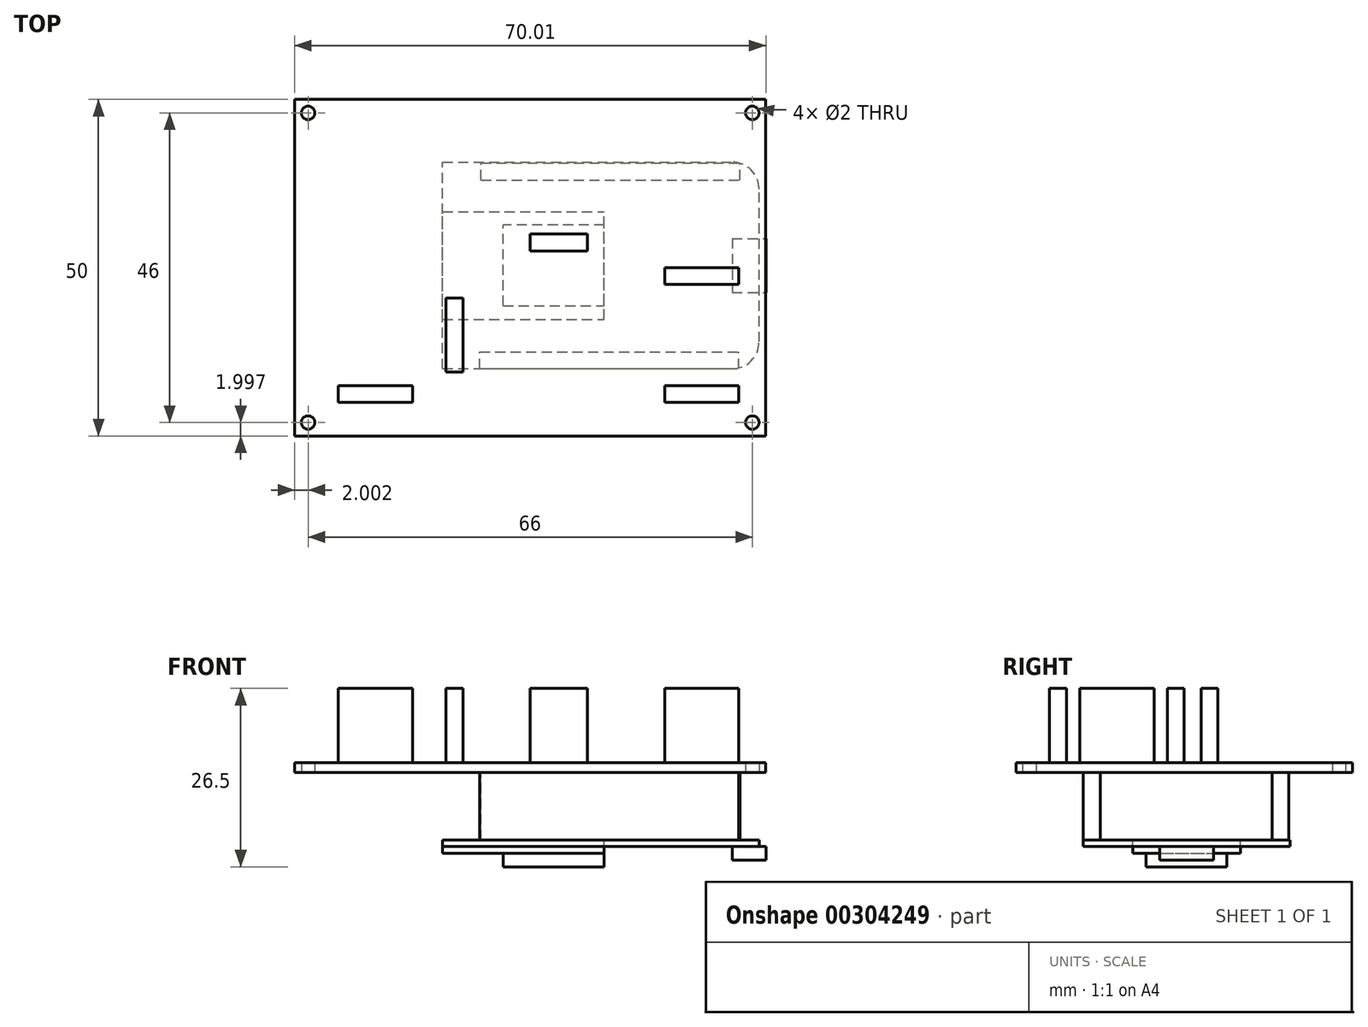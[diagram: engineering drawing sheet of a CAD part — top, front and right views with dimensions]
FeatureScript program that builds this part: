
annotation { "Feature Type Name" : "Feature", "Feature Type Description" : "" }
export const myFeature = defineFeature(function(context is Context, id is Id, definition is map)
    precondition{}
    {
        {
            var Q0;
            Q0=qCreatedBy(makeId("Top.planeOp"),FACE);
            var sketch = newSketch(context, id + "F0", { "sketchPlane" : qUnion([Q0])});
            skLineSegment(sketch, "E0.bottom", {"start": v(-0.7, -1.43) * mm, "end": v(69.3, -1.43) * mm});
            skLineSegment(sketch, "E0.top", {"start": v(-0.7, 48.57) * mm, "end": v(69.3, 48.57) * mm});
            skLineSegment(sketch, "E0.left", {"start": v(-0.7, -1.43) * mm, "end": v(-0.7, 48.57) * mm});
            skLineSegment(sketch, "E0.right", {"start": v(69.3, -1.43) * mm, "end": v(69.3, 48.57) * mm});
            skLineSegment(sketch, "E1.0", {"start": v(1.3, 46.57) * mm, "end": v(67.3, 46.57) * mm, "construction": true});
            skLineSegment(sketch, "E1.1", {"start": v(1.3, 0.57) * mm, "end": v(1.3, 46.57) * mm, "construction": true});
            skLineSegment(sketch, "E1.2", {"start": v(1.3, 0.57) * mm, "end": v(67.3, 0.57) * mm, "construction": true});
            skLineSegment(sketch, "E1.3", {"start": v(67.3, 0.57) * mm, "end": v(67.3, 46.57) * mm, "construction": true});
            skCircle(sketch, "E2", {"center": v(1.3, 0.57) * mm, "radius": 1 * mm});
            skCircle(sketch, "E3", {"center": v(1.3, 46.57) * mm, "radius": 1 * mm});
            skCircle(sketch, "E4", {"center": v(67.3, 46.57) * mm, "radius": 1 * mm});
            skCircle(sketch, "E5", {"center": v(67.3, 0.57) * mm, "radius": 1 * mm});
            skLineSegment(sketch, "E6.bottom", {"start": v(26.8, 8.57) * mm, "end": v(65.3, 8.57) * mm});
            skLineSegment(sketch, "E6.top", {"start": v(26.8, 11.07) * mm, "end": v(65.3, 11.07) * mm});
            skLineSegment(sketch, "E6.left", {"start": v(26.8, 8.57) * mm, "end": v(26.8, 11.07) * mm});
            skLineSegment(sketch, "E6.right", {"start": v(65.3, 8.57) * mm, "end": v(65.3, 11.07) * mm});
            skLineSegment(sketch, "E7.bottom", {"start": v(26.99, 36.6) * mm, "end": v(65.49, 36.6) * mm});
            skLineSegment(sketch, "E7.top", {"start": v(26.99, 39.1) * mm, "end": v(65.49, 39.1) * mm});
            skLineSegment(sketch, "E7.left", {"start": v(26.99, 36.6) * mm, "end": v(26.99, 39.1) * mm});
            skLineSegment(sketch, "E7.right", {"start": v(65.49, 36.6) * mm, "end": v(65.49, 39.1) * mm});
            skSolve(sketch);
        }
        {
            var Q0;
            Q0 = qSketchRegion(id + "F0", true);
            var Q1;
            Q1=makeQuery(id+"F0.imprint","IMPRINT",FACE,{"disambiguationData":[TD([[makeQuery(id+"F0.imprint","IMPRINT",EDGE,{"derivedFrom":sQuery(id+"F0.wireOp",EDGE,"E7.bottom")}),1.0]])]});
            var Q2;
            Q2=makeQuery(id+"F0.imprint","IMPRINT",FACE,{"disambiguationData":[TD([[makeQuery(id+"F0.imprint","IMPRINT",EDGE,{"derivedFrom":sQuery(id+"F0.wireOp",EDGE,"E6.bottom")}),1.0]])]});
            extrude(context, id + "F1", {"entities" : qUnion([Q0, Q1, Q2]), "depth" : 1.5 * mm});
        }
        {
            var Q0;
            Q0=makeQuery(id+"F0.imprint","IMPRINT",FACE,{"disambiguationData":[TD([[makeQuery(id+"F0.imprint","IMPRINT",EDGE,{"derivedFrom":sQuery(id+"F0.wireOp",EDGE,"E6.bottom")}),1.0]])]});
            var Q1;
            Q1=makeQuery(id+"F0.imprint","IMPRINT",FACE,{"disambiguationData":[TD([[makeQuery(id+"F0.imprint","IMPRINT",EDGE,{"derivedFrom":sQuery(id+"F0.wireOp",EDGE,"E7.bottom")}),1.0]])]});
            extrude(context, id + "F2", {"entities" : qUnion([Q0, Q1]), "oppositeDirection" : true, "depth" : 10 * mm});
        }
        {
            var Q0;
            Q0=makeQuery(id+"F2.opExtrude","CAP_FACE",FACE,{"disambiguationData":[OSD([sQuery(id+"F0.wireOp",EDGE,"E6.bottom"),sQuery(id+"F0.wireOp",EDGE,"E6.top"),sQuery(id+"F0.wireOp",EDGE,"E6.left"),sQuery(id+"F0.wireOp",EDGE,"E6.right")])],"isStart":false});
            var sketch = newSketch(context, id + "F3", { "sketchPlane" : qUnion([Q0])});
            skLineSegment(sketch, "E8.bottom", {"start": v(21.3, -8.57) * mm, "end": v(64.3, -8.57) * mm});
            skLineSegment(sketch, "E8.top", {"start": v(21.3, -39.27) * mm, "end": v(64.3, -39.27) * mm});
            skLineSegment(sketch, "E8.left", {"start": v(21.3, -8.57) * mm, "end": v(21.3, -39.27) * mm});
            skLineSegment(sketch, "E8.right", {"start": v(68.3, -12.57) * mm, "end": v(68.3, -35.27) * mm});
            skPoint(sketch, "E9.visualSharp", {"position": v(21.3, -8.57) * mm});
            skPoint(sketch, "E10.visualSharp", {"position": v(68.3, -8.57) * mm});
            skArc(sketch, "E10.filletArc", {"start": v(68.3, -12.57) * mm, "mid": v(67.13, -9.74) * mm, "end": v(64.3, -8.57) * mm});
            skPoint(sketch, "E11.visualSharp", {"position": v(68.3, -39.27) * mm});
            skArc(sketch, "E11.filletArc", {"start": v(64.3, -39.27) * mm, "mid": v(67.13, -38.1) * mm, "end": v(68.3, -35.27) * mm});
            skLineSegment(sketch, "E12.bottom", {"start": v(21.3, -15.92) * mm, "end": v(45.3, -15.92) * mm});
            skLineSegment(sketch, "E12.top", {"start": v(21.3, -31.92) * mm, "end": v(45.3, -31.92) * mm});
            skLineSegment(sketch, "E12.left", {"start": v(21.3, -15.92) * mm, "end": v(21.3, -31.92) * mm});
            skLineSegment(sketch, "E12.right", {"start": v(45.3, -15.92) * mm, "end": v(45.3, -31.92) * mm});
            skPoint(sketch, "E13", {"position": v(21.3, -23.92) * mm});
            skPoint(sketch, "E14", {"position": v(68.3, -23.92) * mm});
            skSolve(sketch);
        }
        {
            var Q0;
            Q0=makeQuery(id+"F3.imprint","IMPRINT",FACE,{"disambiguationData":[TD([[makeQuery(id+"F3.imprint","IMPRINT",EDGE,{"derivedFrom":sQuery(id+"F3.wireOp",EDGE,"E8.top")}),1.0]])]});
            var Q1;
            {var subQ1=makeQuery(id+"F2.opExtrude","CAP_EDGE",EDGE,{"disambiguationData":[OSD([sQuery(id+"F0.wireOp",EDGE,"E6.top")])],"isStart":false});Q1=makeQuery(id+"F3.imprint","IMPRINT",FACE,{"disambiguationData":[TD([[makeQuery(id+"F3.imprint","IMPRINT",EDGE,{"derivedFrom":subQ1}),1.0]])]});}
            var Q2;
            Q2=makeQuery(id+"F3.imprint","IMPRINT",FACE,{"disambiguationData":[TD([[makeQuery(id+"F3.imprint","IMPRINT",EDGE,{"derivedFrom":sQuery(id+"F3.wireOp",EDGE,"E12.bottom")}),-1.0]])]});
            extrude(context, id + "F4", {"entities" : qUnion([Q0, Q1, Q2]), "depth" : 1 * mm});
        }
        {
            var Q0;
            Q0=makeQuery(id+"F3.imprint","IMPRINT",FACE,{"disambiguationData":[TD([[makeQuery(id+"F3.imprint","IMPRINT",EDGE,{"derivedFrom":sQuery(id+"F3.wireOp",EDGE,"E12.bottom")}),-1.0]])]});
            extrude(context, id + "F5", {"entities" : qUnion([Q0]), "depth" : 2 * mm});
        }
        {
            var Q0;
            Q0=makeQuery(id+"F5.opExtrude","CAP_FACE",FACE,{"disambiguationData":[OSD([sQuery(id+"F3.wireOp",EDGE,"E12.bottom"),sQuery(id+"F3.wireOp",EDGE,"E12.top"),sQuery(id+"F3.wireOp",EDGE,"E12.left"),sQuery(id+"F3.wireOp",EDGE,"E12.right")])],"isStart":false});
            var sketch = newSketch(context, id + "F6", { "sketchPlane" : qUnion([Q0])});
            skLineSegment(sketch, "E15.top", {"start": v(45.3, -29.92) * mm, "end": v(30.3, -29.92) * mm});
            skLineSegment(sketch, "E15.left", {"start": v(45.3, -17.92) * mm, "end": v(45.3, -29.92) * mm});
            skLineSegment(sketch, "E15.right", {"start": v(30.3, -17.92) * mm, "end": v(30.3, -29.92) * mm});
            skPoint(sketch, "E16", {"position": v(45.3, -23.92) * mm});
            skPoint(sketch, "E17", {"position": v(30.3, -23.92) * mm});
            skLineSegment(sketch, "E18", {"start": v(30.3, -17.92) * mm, "end": v(45.3, -17.92) * mm});
            skSolve(sketch);
        }
        {
            var Q0;
            Q0 = qSketchRegion(id + "F6", true);
            extrude(context, id + "F7", {"entities" : qUnion([Q0]), "depth" : 2 * mm});
        }
        {
            var Q0;
            Q0=makeQuery(id+"F5.opExtrude","CAP_FACE",FACE,{"disambiguationData":[OSD([sQuery(id+"F3.wireOp",EDGE,"E12.bottom"),sQuery(id+"F3.wireOp",EDGE,"E12.top"),sQuery(id+"F3.wireOp",EDGE,"E12.left"),sQuery(id+"F3.wireOp",EDGE,"E12.right")])],"isStart":false});
            var sketch = newSketch(context, id + "F8", { "sketchPlane" : qUnion([Q0])});
            skLineSegment(sketch, "E19.bottom", {"start": v(64.31, -28.31) * mm, "end": v(69.31, -28.31) * mm});
            skLineSegment(sketch, "E19.top", {"start": v(64.31, -20.31) * mm, "end": v(69.31, -20.31) * mm});
            skLineSegment(sketch, "E19.right", {"start": v(69.31, -28.31) * mm, "end": v(69.31, -20.31) * mm});
            skLineSegment(sketch, "E20.0", {"start": v(64.31, -28.31) * mm, "end": v(64.31, -20.31) * mm});
            skPoint(sketch, "E21", {"position": v(69.31, -23.95) * mm});
            skSolve(sketch);
        }
        {
            var Q0;
            Q0 = qSketchRegion(id + "F8", true);
            extrude(context, id + "F9", {"entities" : qUnion([Q0]), "depth" : 2 * mm});
        }
        {
            var Q0;
            Q0=makeQuery(id+"F1.opExtrude","CAP_FACE",FACE,{"disambiguationData":[OSD([sQuery(id+"F0.wireOp",EDGE,"E0.bottom"),sQuery(id+"F0.wireOp",EDGE,"E0.top"),sQuery(id+"F0.wireOp",EDGE,"E0.left"),sQuery(id+"F0.wireOp",EDGE,"E0.right"),sQuery(id+"F0.wireOp",EDGE,"E2"),sQuery(id+"F0.wireOp",EDGE,"E3"),sQuery(id+"F0.wireOp",EDGE,"E4"),sQuery(id+"F0.wireOp",EDGE,"E5")])],"isStart":false});
            var sketch = newSketch(context, id + "F10", { "sketchPlane" : qUnion([Q0])});
            skLineSegment(sketch, "E22.bottom", {"start": v(54.3, 6.07) * mm, "end": v(65.3, 6.07) * mm});
            skLineSegment(sketch, "E22.top", {"start": v(54.3, 3.57) * mm, "end": v(65.3, 3.57) * mm});
            skLineSegment(sketch, "E22.left", {"start": v(54.3, 6.07) * mm, "end": v(54.3, 3.57) * mm});
            skLineSegment(sketch, "E22.right", {"start": v(65.3, 6.07) * mm, "end": v(65.3, 3.57) * mm});
            skLineSegment(sketch, "E23.bottom", {"start": v(54.3, 23.57) * mm, "end": v(65.3, 23.57) * mm});
            skLineSegment(sketch, "E23.top", {"start": v(54.3, 21.07) * mm, "end": v(65.3, 21.07) * mm});
            skLineSegment(sketch, "E23.left", {"start": v(54.3, 23.57) * mm, "end": v(54.3, 21.07) * mm});
            skLineSegment(sketch, "E23.right", {"start": v(65.3, 23.57) * mm, "end": v(65.3, 21.07) * mm});
            skLineSegment(sketch, "E24.bottom", {"start": v(5.8, 3.57) * mm, "end": v(16.8, 3.57) * mm});
            skLineSegment(sketch, "E24.top", {"start": v(5.8, 6.07) * mm, "end": v(16.8, 6.07) * mm});
            skLineSegment(sketch, "E24.left", {"start": v(5.8, 3.57) * mm, "end": v(5.8, 6.07) * mm});
            skLineSegment(sketch, "E24.right", {"start": v(16.8, 3.57) * mm, "end": v(16.8, 6.07) * mm});
            skLineSegment(sketch, "E25.bottom", {"start": v(21.8, 19.07) * mm, "end": v(24.3, 19.07) * mm});
            skLineSegment(sketch, "E25.top", {"start": v(21.8, 8.07) * mm, "end": v(24.3, 8.07) * mm});
            skLineSegment(sketch, "E25.left", {"start": v(21.8, 19.07) * mm, "end": v(21.8, 8.07) * mm});
            skLineSegment(sketch, "E25.right", {"start": v(24.3, 19.07) * mm, "end": v(24.3, 8.07) * mm});
            skLineSegment(sketch, "E26.bottom", {"start": v(34.3, 28.57) * mm, "end": v(42.8, 28.57) * mm});
            skLineSegment(sketch, "E26.top", {"start": v(34.3, 26.07) * mm, "end": v(42.8, 26.07) * mm});
            skLineSegment(sketch, "E26.left", {"start": v(34.3, 28.57) * mm, "end": v(34.3, 26.07) * mm});
            skLineSegment(sketch, "E26.right", {"start": v(42.8, 28.57) * mm, "end": v(42.8, 26.07) * mm});
            skSolve(sketch);
        }
        {
            var Q0;
            Q0=makeQuery(id+"F10.imprint","IMPRINT",FACE,{"disambiguationData":[TD([[makeQuery(id+"F10.imprint","IMPRINT",EDGE,{"derivedFrom":sQuery(id+"F10.wireOp",EDGE,"E26.bottom")}),-1.0]])]});
            var Q1;
            Q1=makeQuery(id+"F10.imprint","IMPRINT",FACE,{"disambiguationData":[TD([[makeQuery(id+"F10.imprint","IMPRINT",EDGE,{"derivedFrom":sQuery(id+"F10.wireOp",EDGE,"E23.bottom")}),-1.0]])]});
            var Q2;
            Q2=makeQuery(id+"F10.imprint","IMPRINT",FACE,{"disambiguationData":[TD([[makeQuery(id+"F10.imprint","IMPRINT",EDGE,{"derivedFrom":sQuery(id+"F10.wireOp",EDGE,"E22.bottom")}),-1.0]])]});
            var Q3;
            Q3=makeQuery(id+"F10.imprint","IMPRINT",FACE,{"disambiguationData":[TD([[makeQuery(id+"F10.imprint","IMPRINT",EDGE,{"derivedFrom":sQuery(id+"F10.wireOp",EDGE,"E25.bottom")}),-1.0]])]});
            var Q4;
            Q4=makeQuery(id+"F10.imprint","IMPRINT",FACE,{"disambiguationData":[TD([[makeQuery(id+"F10.imprint","IMPRINT",EDGE,{"derivedFrom":sQuery(id+"F10.wireOp",EDGE,"E24.bottom")}),1.0]])]});
            extrude(context, id + "F11", {"entities" : qUnion([Q0, Q1, Q2, Q3, Q4]), "depth" : 11 * mm});
        }
        {
            var Q0;
            Q0=makeQuery(id+"F9.opExtrude","SWEPT_BODY",BODY,{"disambiguationData":[OSD([sQuery(id+"F8.wireOp",EDGE,"E19.bottom"),sQuery(id+"F8.wireOp",EDGE,"E19.top"),sQuery(id+"F8.wireOp",EDGE,"E19.right"),sQuery(id+"F8.wireOp",EDGE,"E20.0")])]});
            var Q1;
            Q1=makeQuery(id+"F9.opExtrude","CAP_VERTEX",VERTEX,{"disambiguationData":[OSD([sQuery(id+"F8.wireOp",EDGE,"E19.top"),sQuery(id+"F8.wireOp",EDGE,"E19.right")])],"isStart":true});
            var Q2;
            Q2=makeQuery(id+"F4.opExtrude","CAP_EDGE",EDGE,{"disambiguationData":[OSD([sQuery(id+"F3.wireOp",EDGE,"E8.right")])],"isStart":false});
            transform(context, id + "F12", {"entities" : qUnion([Q0]), "transformType" : TransformType.TRANSLATION_3D, "dx" : 0 * mm, "dy" : 0 * mm, "dz" : 1 * mm, "makeCopy" : false});
        }
        {
            var Q0;
            Q0=makeQuery(id+"F9.opExtrude","SWEPT_BODY",BODY,{"disambiguationData":[OSD([sQuery(id+"F8.wireOp",EDGE,"E19.bottom"),sQuery(id+"F8.wireOp",EDGE,"E19.top"),sQuery(id+"F8.wireOp",EDGE,"E19.right"),sQuery(id+"F8.wireOp",EDGE,"E20.0")])]});
            transform(context, id + "F13", {"entities" : qUnion([Q0]), "transformType" : TransformType.TRANSLATION_3D, "dx" : 0 * mm, "dy" : -0.4 * mm, "dz" : 0 * mm, "makeCopy" : false});
        }
    });
